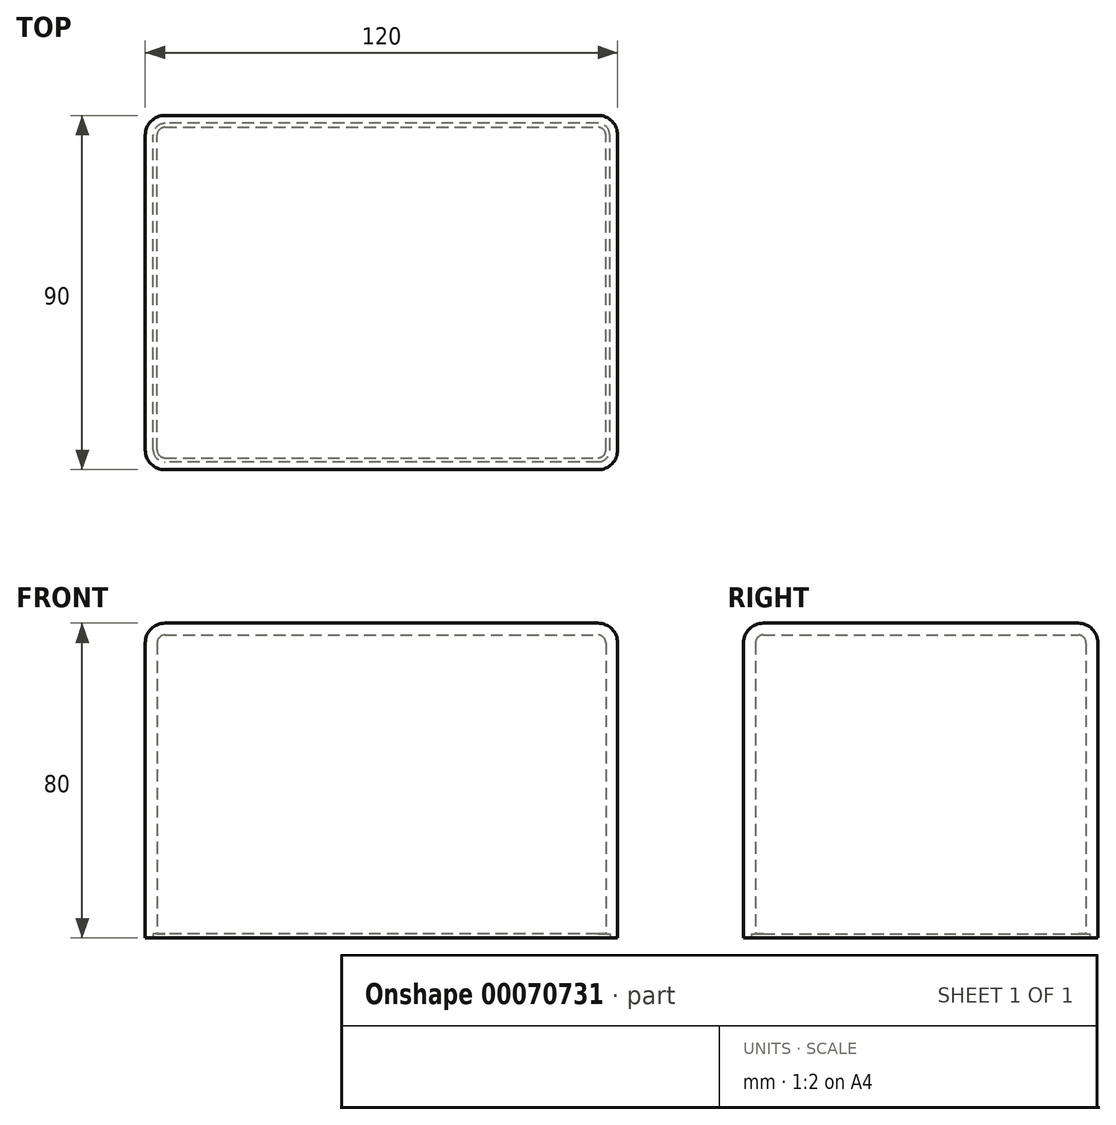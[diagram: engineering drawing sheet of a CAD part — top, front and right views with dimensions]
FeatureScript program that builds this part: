
annotation { "Feature Type Name" : "Feature", "Feature Type Description" : "" }
export const myFeature = defineFeature(function(context is Context, id is Id, definition is map)
    precondition{}
    {
        {
            var Q0;
            Q0=qCreatedBy(makeId("Top.planeOp"),FACE);
            var sketch = newSketch(context, id + "F0", { "sketchPlane" : qUnion([Q0])});
            skLineSegment(sketch, "E0.rect.bottom", {"start": v(60, 45) * mm, "end": v(-60, 45) * mm});
            skLineSegment(sketch, "E0.rect.top", {"start": v(60, -45) * mm, "end": v(-60, -45) * mm});
            skLineSegment(sketch, "E0.rect.left", {"start": v(60, 45) * mm, "end": v(60, -45) * mm});
            skLineSegment(sketch, "E0.rect.right", {"start": v(-60, 45) * mm, "end": v(-60, -45) * mm});
            skPoint(sketch, "E0.rect.middle", {"position": v(0, 0) * mm});
            skSolve(sketch);
        }
        {
            var Q0;
            Q0 = qSketchRegion(id + "F0", true);
            extrude(context, id + "F1", {"entities" : qUnion([Q0]), "depth" : 80 * mm});
        }
        {
            var Q0;
            Q0=makeQuery(id+"F1.opExtrude","SWEPT_EDGE",EDGE,{"disambiguationData":[OSD([sQuery(id+"F0.wireOp",EDGE,"E0.rect.top"),sQuery(id+"F0.wireOp",EDGE,"E0.rect.left")])]});
            var Q1;
            Q1=makeQuery(id+"F1.opExtrude","SWEPT_EDGE",EDGE,{"disambiguationData":[OSD([sQuery(id+"F0.wireOp",EDGE,"E0.rect.top"),sQuery(id+"F0.wireOp",EDGE,"E0.rect.right")])]});
            var Q2;
            Q2=makeQuery(id+"F1.opExtrude","CAP_EDGE",EDGE,{"disambiguationData":[OSD([sQuery(id+"F0.wireOp",EDGE,"E0.rect.top")])],"isStart":false});
            var Q3;
            Q3=makeQuery(id+"F1.opExtrude","CAP_EDGE",EDGE,{"disambiguationData":[OSD([sQuery(id+"F0.wireOp",EDGE,"E0.rect.left")])],"isStart":false});
            var Q4;
            Q4=makeQuery(id+"F1.opExtrude","SWEPT_EDGE",EDGE,{"disambiguationData":[OSD([sQuery(id+"F0.wireOp",EDGE,"E0.rect.bottom"),sQuery(id+"F0.wireOp",EDGE,"E0.rect.left")])]});
            var Q5;
            Q5=makeQuery(id+"F1.opExtrude","CAP_EDGE",EDGE,{"disambiguationData":[OSD([sQuery(id+"F0.wireOp",EDGE,"E0.rect.bottom")])],"isStart":false});
            var Q6;
            Q6=makeQuery(id+"F1.opExtrude","CAP_EDGE",EDGE,{"disambiguationData":[OSD([sQuery(id+"F0.wireOp",EDGE,"E0.rect.right")])],"isStart":false});
            var Q7;
            Q7=makeQuery(id+"F1.opExtrude","SWEPT_EDGE",EDGE,{"disambiguationData":[OSD([sQuery(id+"F0.wireOp",EDGE,"E0.rect.bottom"),sQuery(id+"F0.wireOp",EDGE,"E0.rect.right")])]});
            fillet(context, id + "F2", {"entities" : qUnion([Q0, Q1, Q2, Q3, Q4, Q5, Q6, Q7]), "radius" : 5 * mm, "tangentPropagation" : true, "allowEdgeOverflow" : false});
        }
        {
            var Q0;
            Q0=makeQuery(id+"F1.opExtrude","CAP_FACE",FACE,{"disambiguationData":[OSD([sQuery(id+"F0.wireOp",EDGE,"E0.rect.bottom"),sQuery(id+"F0.wireOp",EDGE,"E0.rect.top"),sQuery(id+"F0.wireOp",EDGE,"E0.rect.left"),sQuery(id+"F0.wireOp",EDGE,"E0.rect.right")])],"isStart":true});
            shell(context, id + "F3", {"entities" : qUnion([Q0]), "thickness" : 3 * mm});
        }
        {
            var Q0;
            Q0=makeQuery(id+"F1.opExtrude","CAP_FACE",FACE,{"disambiguationData":[OSD([sQuery(id+"F0.wireOp",EDGE,"E0.rect.bottom"),sQuery(id+"F0.wireOp",EDGE,"E0.rect.top"),sQuery(id+"F0.wireOp",EDGE,"E0.rect.left"),sQuery(id+"F0.wireOp",EDGE,"E0.rect.right")])],"isStart":true});
            var sketch = newSketch(context, id + "F4", { "sketchPlane" : qUnion([Q0])});
            skLineSegment(sketch, "E1.rect.bottom", {"start": v(55, 43) * mm, "end": v(-55, 43) * mm});
            skLineSegment(sketch, "E1.rect.top", {"start": v(55, -43) * mm, "end": v(-55, -43) * mm});
            skLineSegment(sketch, "E1.rect.left", {"start": v(58, 40) * mm, "end": v(58, -40) * mm});
            skLineSegment(sketch, "E1.rect.right", {"start": v(-58, 40) * mm, "end": v(-58, -40) * mm});
            skPoint(sketch, "E1.rect.middle", {"position": v(0, 0) * mm});
            skPoint(sketch, "E2.visualSharp", {"position": v(58, 43) * mm});
            skArc(sketch, "E2.filletArc", {"start": v(58, 40) * mm, "mid": v(57.12, 42.12) * mm, "end": v(55, 43) * mm});
            skPoint(sketch, "E3.visualSharp", {"position": v(-58, 43) * mm});
            skArc(sketch, "E3.filletArc", {"start": v(-55, 43) * mm, "mid": v(-57.12, 42.12) * mm, "end": v(-58, 40) * mm});
            skPoint(sketch, "E4.visualSharp", {"position": v(-58, -43) * mm});
            skArc(sketch, "E4.filletArc", {"start": v(-58, -40) * mm, "mid": v(-57.12, -42.12) * mm, "end": v(-55, -43) * mm});
            skPoint(sketch, "E5.visualSharp", {"position": v(58, -43) * mm});
            skArc(sketch, "E5.filletArc", {"start": v(55, -43) * mm, "mid": v(57.12, -42.12) * mm, "end": v(58, -40) * mm});
            skSolve(sketch);
        }
        {
            var Q0;
            Q0 = qSketchRegion(id + "F4", true);
            extrude(context, id + "F5", {"entities" : qUnion([Q0]), "operationType" : NewBodyOperationType.REMOVE, "oppositeDirection" : true, "depth" : 1 * mm});
        }
    });
